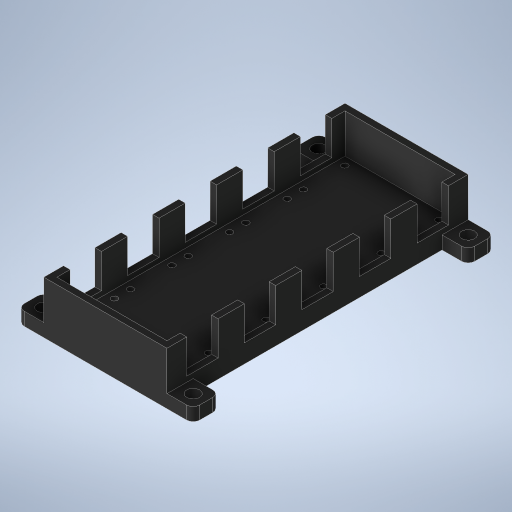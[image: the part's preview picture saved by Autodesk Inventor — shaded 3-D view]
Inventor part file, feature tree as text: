
AUTODESK INVENTOR PART (.ipt)
format: ipt  version: 2024 (Build 280153000, 153)  size: 948,736 bytes
history: native  units: in
note: dims shown in document units (in); Inventor stores cm internally (conversion verified against a paired STEP export)
features: projected_geometry x13, extrude x5, sketch x4
ambient origin geometry x8: Origin, YZ Plane, XZ Plane, XY Plane, X Axis, Y Axis, Z Axis, Center Point
bodies: Solid1 (feature_tree)
feature tree (22):
  extrude  "Extrusion1"  Depth=1.0in
  extrude  "Extrusion7"  Depth=0.0742in
  extrude  "Extrusion8"  Depth=0.2in
  extrude  "Extrusion9"  Depth=0.125in
  extrude  "Extrusion10"  Depth=0.125in
  sketch  "Sketch10"  dims[d0=1.0in d1=2.0in]
  projected_geometry  "Projected Loop17"
  sketch  "Sketch11"  dims[d2=0.12in d3=0.0742in]
  projected_geometry  "Projected Loop18"
  projected_geometry  "Projected Loop19"
  projected_geometry  "Projected Loop20"
  projected_geometry  "Projected Loop21"
  projected_geometry  "Projected Loop22"
  projected_geometry  "Projected Loop23"
  projected_geometry  "Projected Loop24"
  projected_geometry  "Projected Loop25"
  projected_geometry  "Projected Loop26"
  projected_geometry  "Projected Loop27"
  sketch  "Sketch12"  dims[d4=0.1742in d5=0.2in]
  projected_geometry  "Projected Loop28"
  sketch  "Sketch13"  dims[d6=0.2in d7=0.201in d8=0.799in d9=0.8in d10=0.8in d11=0.3in d12=0.4967in d13=0.4267in d14=0.1217in d15=0.3933in d16=1.3983in d17=1.0933in d18=0.7933in d19=0.4967in d20=0.0in d21=1.5033in d22=0.0in d23=0.0in d24=0.0742in d25=0.3in d26=0.0742in d27=0.105in d28=0.3949in d29=0.105in d30=1.4015in d31=0.0in d32=0.1742in d33=0.3in d34=0.1742in d35=0.4267in d36=0.2in d37=0.1217in d38=0.2in d39=0.2in d40=1.0933in d41=0.2in d42=1.3983in d43=0.3933in d44=0.201in d45=0.201in d46=1.0933in d47=0.3933in d48=0.799in d49=1.0933in d50=0.799in d51=0.4267in d52=0.8in d53=0.1217in d54=0.8in d55=0.8in d56=1.0933in d57=0.8in d58=1.3983in d59=0.895in d60=0.3949in d61=0.895in d62=1.4015in d63=1.0in d64=0.4967in d65=1.5033in d66=1.0in d67=1.0in d68=2.0in d69=0.12in d70=0.0742in d71=0.1742in d72=0.2in d73=0.2in d74=0.201in d75=0.799in d76=0.8in d77=0.8in d78=0.3in d79=0.4967in d80=0.4267in d81=0.1217in d82=0.3933in d83=1.3983in d84=1.0933in d85=0.7933in d86=0.4967in d87=0.0in d88=1.5033in d89=0.0in d90=0.0in d91=0.0742in d92=0.3in d93=0.0742in d94=0.105in d95=0.3949in d96=0.105in d97=1.4015in d98=0.0in d99=0.1742in d100=0.3in d101=0.1742in d102=0.4267in d103=0.2in d104=0.1217in d105=0.2in d106=0.2in d107=1.0933in d108=0.2in d109=1.3983in d110=0.3933in d111=0.201in d112=0.201in d113=1.0933in d114=0.3933in d115=0.799in d116=1.0933in d117=0.799in d118=0.4267in d119=0.8in d120=0.1217in d121=0.8in d122=0.8in d123=1.0933in d124=0.8in d125=1.3983in d126=0.895in d127=0.3949in d128=0.895in d129=1.4015in d130=1.0in d131=0.4967in d132=1.5033in d133=1.0in d134=1.0in d135=2.0in d136=0.12in d137=0.0742in d138=0.1742in d139=0.2in d140=0.2in d141=0.201in d142=0.799in d143=0.8in d144=0.8in d145=0.3in d146=0.4967in d147=0.4267in d148=0.1217in d149=0.3933in d150=1.3983in d151=1.0933in d152=0.7933in d153=0.4967in d154=0.0in d155=1.5033in d156=0.0in d157=0.0in d158=0.0742in d159=0.3in d160=0.0742in d161=0.105in d162=0.3949in d163=0.105in d164=1.4015in d165=0.0in d166=0.1742in d167=0.3in d168=0.1742in d169=0.4267in d170=0.2in d171=0.1217in d172=0.2in d173=0.2in d174=1.0933in d175=0.2in d176=1.3983in d177=0.3933in d178=0.201in d179=0.201in d180=1.0933in d181=0.3933in d182=0.799in d183=1.0933in d184=0.799in d185=0.4267in d186=0.8in d187=0.1217in d188=0.8in d189=0.8in d190=1.0933in d191=0.8in d192=1.3983in d193=0.895in d194=0.3949in d195=0.895in d196=1.4015in d197=1.0in d198=0.4967in d199=1.5033in d200=1.0in d201=1.0in d202=2.0in d203=0.12in d204=0.0742in d205=0.1742in d206=0.2in d207=0.2in d208=0.201in d209=0.799in d210=0.8in d211=0.8in d212=0.3in d213=0.4967in d214=0.4267in d215=0.1217in d216=0.3933in d217=1.3983in d218=1.0933in d219=0.7933in d220=0.4967in d221=0.0in d222=1.5033in d223=0.0in d224=0.0in d225=0.0742in d226=0.3in d227=0.0742in d228=0.105in d229=0.3949in d230=0.105in d231=1.4015in d232=0.0in d233=0.1742in d234=0.3in d235=0.1742in d236=0.4267in d237=0.2in d238=0.1217in d239=0.2in d240=0.2in d241=1.0933in d242=0.2in d243=1.3983in d244=0.3933in d245=0.201in d246=0.201in d247=1.0933in d248=0.3933in d249=0.799in d250=1.0933in d251=0.799in d252=0.4267in d253=0.8in d254=0.1217in d255=0.8in d256=0.8in d257=1.0933in d258=0.8in d259=1.3983in d260=0.895in d261=0.3949in d262=0.895in d263=1.4015in d264=1.0in d265=0.4967in d266=1.5033in d267=1.0in d268=1.0in d269=2.0in d270=0.12in d271=0.0742in d272=0.1742in d273=0.2in d274=0.2in d275=0.201in d276=0.799in d277=0.8in d278=0.8in d279=0.3in d280=0.4967in d281=0.4267in d282=0.1217in d283=0.3933in d284=1.3983in d285=1.0933in d286=0.7933in d287=0.4967in d288=0.0in d289=1.5033in d290=0.0in d291=0.0in d292=0.0742in d293=0.3in d294=0.0742in d295=0.105in d296=0.3949in d297=0.105in d298=1.4015in d299=0.0in d300=0.1742in d301=0.3in d302=0.1742in d303=0.4267in d304=0.2in d305=0.1217in d306=0.2in d307=0.2in d308=1.0933in d309=0.2in d310=1.3983in d311=0.3933in d312=0.201in d313=0.201in d314=1.0933in d315=0.3933in d316=0.799in d317=1.0933in d318=0.799in d319=0.4267in d320=0.8in d321=0.1217in d322=0.8in d323=0.8in d324=1.0933in d325=0.8in d326=1.3983in d327=0.895in d328=0.3949in d329=0.895in d330=1.4015in d331=1.0in d332=0.4967in d333=1.5033in d334=1.0in d335=0.1in d336=0.1in d337=0.1in d338=0.1in d339=0.03in d340=0.03in d341=0.125in d342=0.0in d367=0.125in d368=0.75in d369=0.0in d370=0.1in d371=0.0in d372=0.5in d373=0.5in d374=0.5in d375=0.5in d376=0.25in d377=0.25in d378=0.125in d379=0.125in d380=0.0in d381=0.125in d382=0.125in d383=0.0in]
  projected_geometry  "Projected Loop29"
